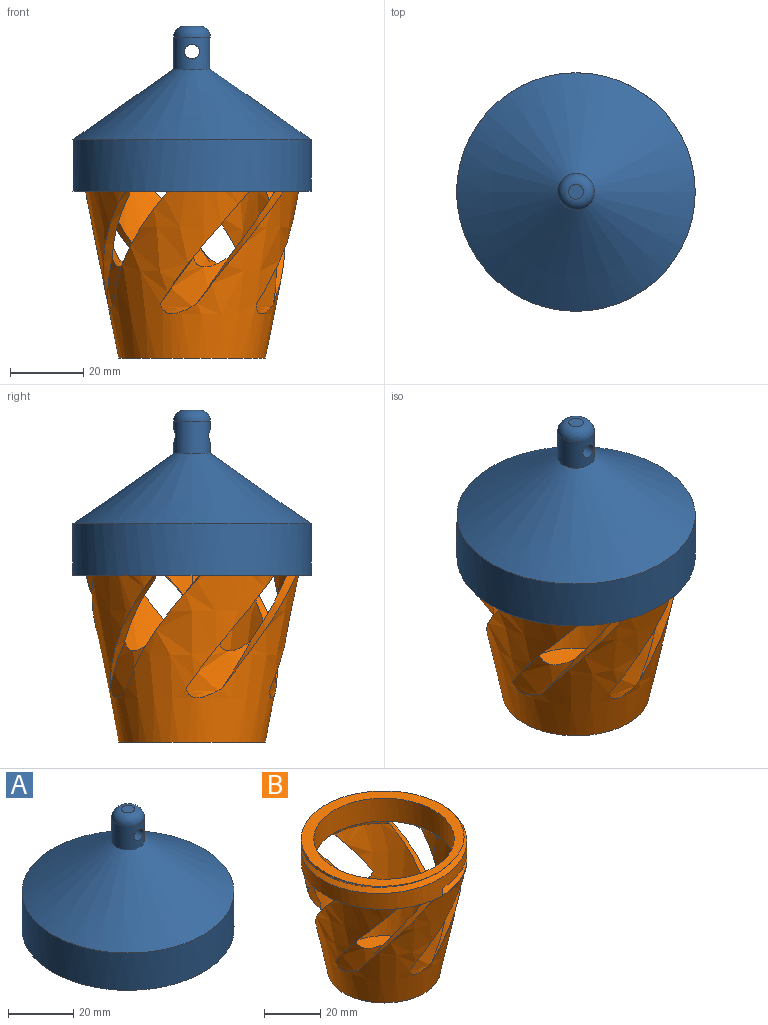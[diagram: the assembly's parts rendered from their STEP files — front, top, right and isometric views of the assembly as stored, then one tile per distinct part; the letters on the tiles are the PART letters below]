
ASSEMBLY  parts=2 mates=1
PART A: 13 faces, bbox 65.6x65.6x47.4 mm
  f0: cone r=2.5mm half-angle=55deg, axis (0,0,-1), area 3955mm2, adj f4,f9
  f1: cone r=30.5mm half-angle=55deg, axis (0,0,-1), area 3479.6mm2, adj f6,f8
  f2: bspline ~61x61mm, area 524.1mm2, adj f3,f5,f6,f7
  f3: bspline ~61x61mm, area 458.8mm2, adj f2,f5,f6,f7
  f4: cylinder r=32.5mm len=65mm, axis (0,0,-1), area 2857.6mm2, adj f0,f5
  f5: plane 65.61x65.61mm, normal (0,0,-1), area 442mm2, adj f2,f3,f4,f6
  f6: cylinder r=30.5mm len=61mm, axis (0,0,-1), area 1588.6mm2, adj f1,f2,f3,f5,f7
  f7: plane 2.8x1.4mm, normal (0,1,0), area 2mm2, adj f2,f3,f6
  f8: plane 9.59x9.59mm, normal (0,0,-1), area 72.2mm2, adj f1
  f9: cylinder r=5mm len=10mm, axis (0,0,-1), area 249.3mm2, adj f0,f11,f12
  f10: plane 4x4mm, normal (0,0,1), area 12.6mm2, adj f11
  f11: torus R=2mm, axis (0,0,1), area 115.8mm2, adj f9,f10
  f12: cylinder r=2mm len=10mm, axis (0,-1,0), area 125.7mm2, adj f9
PART B: 37 faces, bbox 67.2x67.2x60.7 mm
  f0: plane 12.06x11.2mm, normal (0,0,-1), area 55.1mm2, adj f22,f23,f25,f26
  f1: plane 12.63x10.06mm, normal (0,0,-1), area 55.1mm2, adj f13,f14,f25,f26
  f2: plane 12.9x7.07mm, normal (0,0,-1), area 55.1mm2, adj f16,f17,f25,f26
  f3: plane 12.89x8.68mm, normal (0,0,-1), area 55.1mm2, adj f19,f20,f25,f26
  f4: plane 35.9x35.9mm, normal (0,0,1), area 1012.3mm2, adj f5
  f5: cone r=27.55mm half-angle=11.3deg, axis (0,0,1), area 5007mm2, adj f4,f6,f10,f11,f12,f13,f14,f15
  f6: cone r=27.55mm half-angle=11.3deg, axis (0,0,1), area 29.6mm2, adj f5,f13,f33
  f7: cone r=30mm half-angle=11.3deg, axis (0,0,1), area 5436.9mm2, adj f8,f9,f10,f11,f12,f13,f14,f15
  f8: cone r=30mm half-angle=11.3deg, axis (0,0,1), area 49mm2, adj f7,f13,f25
  f9: plane 40x40mm, normal (0,0,-1), area 1256.6mm2, adj f7
  f10: bspline ~20x18.9mm, area 128mm2, adj f5,f7,f11,f12
  f11: bspline ~40x29.92mm, area 88.7mm2, adj f5,f7,f10,f26,f28,f36
  f12: bspline ~40x35.71mm, area 88.7mm2, adj f5,f7,f10,f26,f28,f35
  f13: bspline ~40x37.73mm, area 88.7mm2, adj f1,f5,f6,f7,f8,f15,f26,f33
  f14: bspline ~40x37.73mm, area 88.7mm2, adj f1,f5,f7,f15,f26,f34
  f15: bspline ~22.22x20mm, area 128.1mm2, adj f5,f7,f13,f14
  f16: bspline ~40x33.16mm, area 88.7mm2, adj f2,f5,f7,f18,f26,f34
  f17: bspline ~40x38.61mm, area 88.7mm2, adj f2,f5,f7,f18,f26,f36
  f18: bspline ~20x18.9mm, area 128mm2, adj f5,f7,f16,f17
  f19: bspline ~40x35.71mm, area 88.7mm2, adj f3,f5,f7,f21,f26,f35
  f20: bspline ~40x29.92mm, area 88.7mm2, adj f3,f5,f7,f21,f26,f32
  f21: bspline ~22.22x20mm, area 128mm2, adj f5,f7,f19,f20
  f22: bspline ~40x38.61mm, area 88.7mm2, adj f0,f5,f7,f24,f26,f32
  f23: bspline ~40x33.16mm, area 88.7mm2, adj f0,f5,f7,f24,f26,f33
  f24: bspline ~23.36x20mm, area 128mm2, adj f5,f7,f22,f23
  f25: cylinder r=29.5mm len=59mm, axis (0,0,-1), area 1230.6mm2, adj f0,f1,f2,f3,f7,f8,f27,f28
  f26: cylinder r=25mm len=50mm, axis (0,0,-1), area 1576.9mm2, adj f0,f1,f2,f3,f11,f12,f13,f14
  f27: plane 59.62x58.45mm, normal (0,0,1), area 712.3mm2, adj f25,f26,f30,f31
  f28: plane 13.23x5.62mm, normal (0,0,-1), area 55.1mm2, adj f11,f12,f25,f26
  f29: plane 3.2x1.6mm, normal (1,0,0), area 2.6mm2, adj f25,f30,f31
  f30: bspline ~59x59mm, area 387.4mm2, adj f25,f27,f29,f31
  f31: bspline ~59x59mm, area 469.9mm2, adj f25,f27,f29,f30
  f32: cone r=26.56mm half-angle=39.3deg, axis (0,0,-1), area 51.3mm2, adj f5,f20,f22,f26
  f33: cone r=26.56mm half-angle=39.3deg, axis (0,0,-1), area 51.3mm2, adj f5,f6,f13,f23,f26
  f34: cone r=26.56mm half-angle=39.3deg, axis (0,0,-1), area 51.3mm2, adj f5,f14,f16,f26
  f35: cone r=26.56mm half-angle=39.3deg, axis (0,0,-1), area 51.3mm2, adj f5,f12,f19,f26
  f36: cone r=26.56mm half-angle=39.3deg, axis (0,0,-1), area 51.3mm2, adj f5,f11,f17,f26
PLACE A t=(-134.88,2.45,32.35)mm
PLACE B t=(-54.88,2.45,-13.15)mm
MATE planar A.f1 <-> B.f26  axis (0,0,-1) through (-54.88,2.45,44.35)mm
